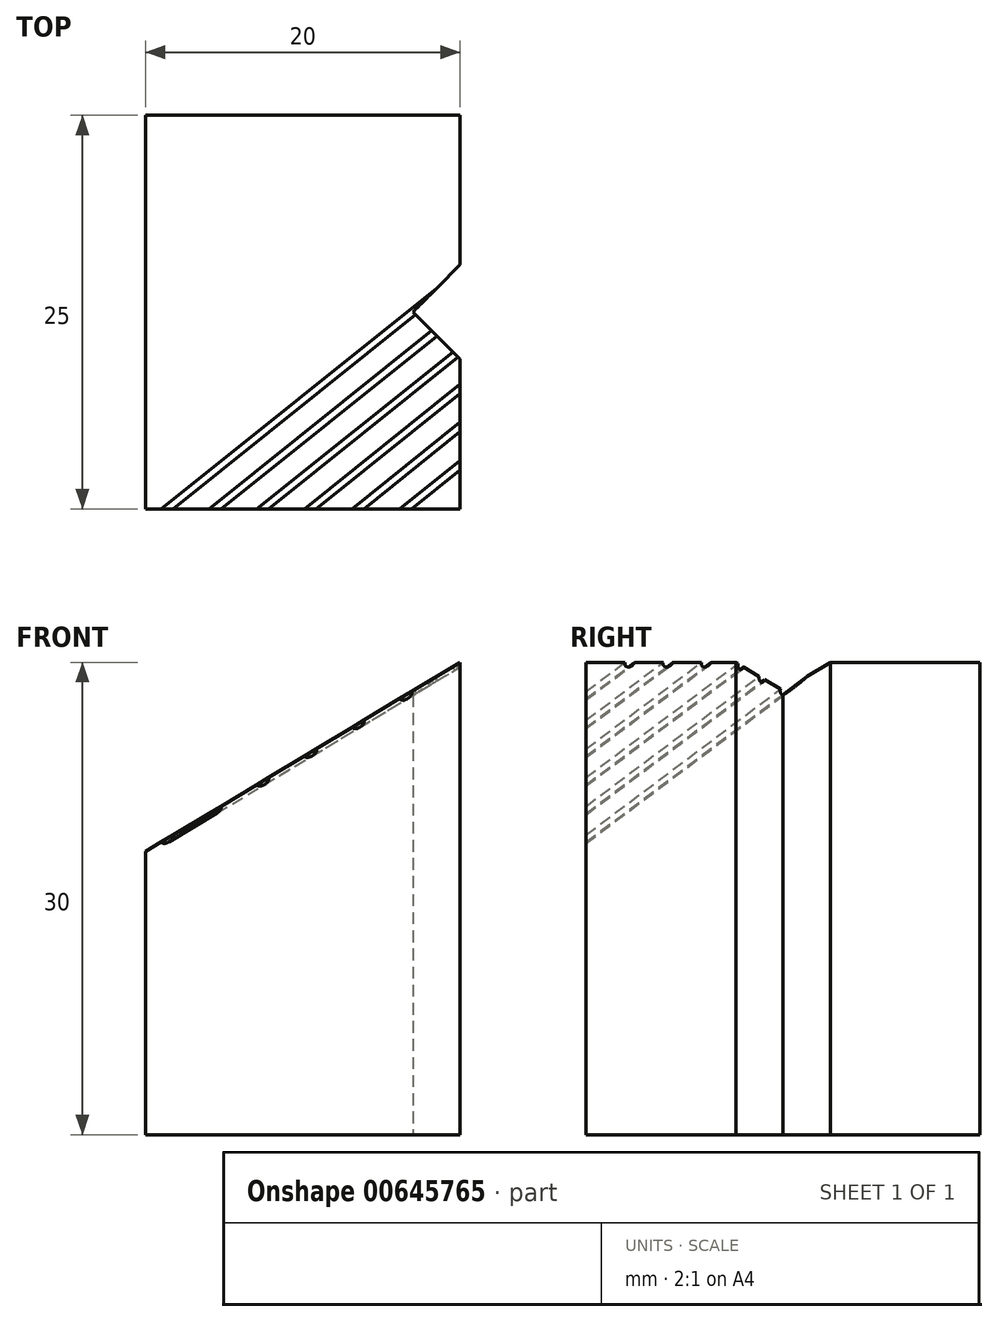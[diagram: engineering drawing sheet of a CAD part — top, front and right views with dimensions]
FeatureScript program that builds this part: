
annotation { "Feature Type Name" : "Feature", "Feature Type Description" : "" }
export const myFeature = defineFeature(function(context is Context, id is Id, definition is map)
    precondition{}
    {
        {
            var Q0;
            Q0=qCreatedBy(makeId("Front.planeOp"),FACE);
            var sketch = newSketch(context, id + "F0", { "sketchPlane" : qUnion([Q0])});
            skLineSegment(sketch, "E0", {"start": v(0, 0) * mm, "end": v(0, 30) * mm});
            skLineSegment(sketch, "E1", {"start": v(0, 30) * mm, "end": v(-20, 17.98) * mm});
            skLineSegment(sketch, "E2", {"start": v(-20, 17.98) * mm, "end": v(-20, 0) * mm});
            skLineSegment(sketch, "E3", {"start": v(-20, 0) * mm, "end": v(0, 0) * mm});
            skSolve(sketch);
        }
        {
            var Q0;
            Q0=qSketchRegion(id+"F0",true);
            extrude(context, id + "F1", {"entities" : qUnion([Q0]), "depth" : 25 * mm, "offsetDistance" : 25 * mm});
        }
        {
            var Q0;
            Q0=makeQuery(id+"F1.opExtrude","SWEPT_FACE",FACE,{"disambiguationData":[OSD([sQuery(id+"F0.wireOp",EDGE,"E3")])]});
            var sketch = newSketch(context, id + "F2", { "sketchPlane" : qUnion([Q0])});
            skLineSegment(sketch, "E4", {"start": v(0, 12.5) * mm, "end": v(-20, 12.5) * mm, "construction": true});
            skLineSegment(sketch, "E5", {"start": v(0, 15.5) * mm, "end": v(-3, 12.5) * mm});
            skLineSegment(sketch, "E6.MirrorCS", {"start": v(0, 9.5) * mm, "end": v(-3, 12.5) * mm});
            skLineSegment(sketch, "E7", {"start": v(0, 15.5) * mm, "end": v(0, 9.5) * mm});
            skLineSegment(sketch, "E8", {"start": v(0, 0) * mm, "end": v(-60.77, 36.51) * mm, "construction": true});
            skPoint(sketch, "E9", {"position": v(-20, 12.02) * mm});
            skSolve(sketch);
        }
        {
            var Q0;
            Q0=qSketchRegion(id+"F2",true);
            extrude(context, id + "F3", {"entities" : qUnion([Q0]), "operationType" : NewBodyOperationType.REMOVE, "endBound" : BoundingType.THROUGH_ALL, "oppositeDirection" : true, "depth" : 25 * mm, "offsetDistance" : 25 * mm});
        }
        {
            var Q0;
            Q0=makeQuery(id+"F1.opExtrude","SWEPT_FACE",FACE,{"disambiguationData":[OSD([sQuery(id+"F0.wireOp",EDGE,"E1")])]});
            var sketch = newSketch(context, id + "F4", { "sketchPlane" : qUnion([Q0])});
            skLineSegment(sketch, "E10", {"start": v(-7.88, -16) * mm, "end": v(15.45, 0) * mm, "construction": true});
            skSolve(sketch);
        }
        {
            var Q0;
            Q0=sQuery(id+"F4.wireOp",EDGE,"E10");
            var Q1;
            Q1=sQuery(id+"F4.wireOp",VERTEX,"E10.end");
            cPlane(context, id + "F5", {"entities" : qUnion([Q0, Q1]), "cplaneType" : CPlaneType.LINE_POINT, "offset" : 25 * mm, "width" : 150 * mm, "height" : 150 * mm});
        }
        {
            var Q0;
            Q0=qCreatedBy(id+"F5.planeOp",FACE);
            var sketch = newSketch(context, id + "F6", { "sketchPlane" : qUnion([Q0])});
            skPoint(sketch, "E11.0", {"position": v(-17.07, 25.72) * mm});
            skCircle(sketch, "E12", {"center": v(-17.07, 25.72) * mm, "radius": 0.25 * mm});
            skCircle(sketch, "E13.1.0.0", {"center": v(-19.07, 25.72) * mm, "radius": 0.25 * mm});
            skCircle(sketch, "E13.2.0.0", {"center": v(-21.07, 25.72) * mm, "radius": 0.25 * mm});
            skCircle(sketch, "E13.3.0.0", {"center": v(-23.07, 25.72) * mm, "radius": 0.25 * mm});
            skCircle(sketch, "E13.4.0.0", {"center": v(-25.07, 25.72) * mm, "radius": 0.25 * mm});
            skLineSegment(sketch, "E13.direction1", {"start": v(-17.07, 25.72) * mm, "end": v(-19.07, 25.72) * mm, "construction": true});
            skCircle(sketch, "E14.0.5.0", {"center": v(-27.07, 25.72) * mm, "radius": 0.25 * mm});
            skSolve(sketch);
        }
        {
            var Q0;
            Q0=qSketchRegion(id+"F6",true);
            extrude(context, id + "F7", {"entities" : qUnion([Q0]), "operationType" : NewBodyOperationType.REMOVE, "endBound" : BoundingType.THROUGH_ALL, "oppositeDirection" : true, "depth" : 25 * mm, "offsetDistance" : 25 * mm});
        }
    });
